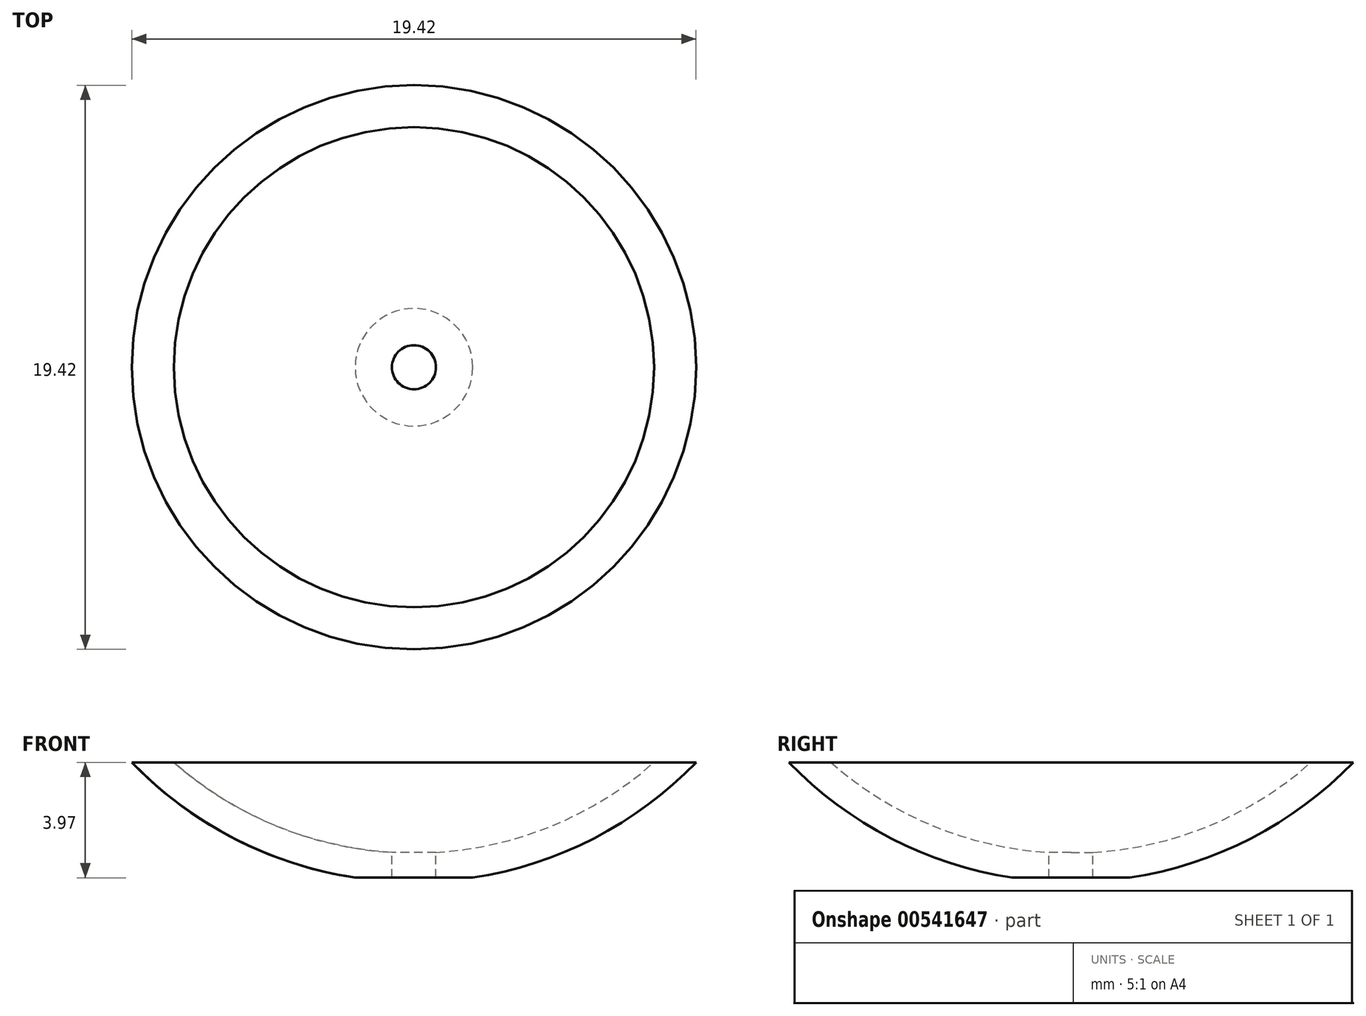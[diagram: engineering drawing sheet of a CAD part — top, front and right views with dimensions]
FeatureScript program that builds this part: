
annotation { "Feature Type Name" : "Feature", "Feature Type Description" : "" }
export const myFeature = defineFeature(function(context is Context, id is Id, definition is map)
    precondition{}
    {
        {
            var Q0;
            Q0=qCreatedBy(makeId("Front.planeOp"),FACE);
            var sketch = newSketch(context, id + "F0", { "sketchPlane" : qUnion([Q0])});
            skCircle(sketch, "E0", {"center": v(0, 0) * mm, "radius": 13.5 * mm});
            skLineSegment(sketch, "E1", {"start": v(0, 13.5) * mm, "end": v(0, -13.5) * mm});
            skSolve(sketch);
        }
        {
            var Q0;
            {var subQ0=sQuery(id+"F0.wireOp",EDGE,"E1");Q0=makeQuery(id+"F0.imprint","IMPRINT",FACE,{"disambiguationData":[TD([[makeQuery(id+"F0.imprint","IMPRINT",EDGE,{"derivedFrom":subQ0}),1.0]])]});}
            var Q1;
            Q1=sQuery(id+"F0.wireOp",EDGE,"E1");
            revolve(context, id + "F1", {"entities" : qUnion([Q0]), "axis" : qUnion([Q1]), "revolveType" : RevolveType.FULL});
        }
        {
            var Q0;
            Q0=qCreatedBy(makeId("Front.planeOp"),FACE);
            var sketch = newSketch(context, id + "F2", { "sketchPlane" : qUnion([Q0])});
            skLineSegment(sketch, "E2.bottom", {"start": v(-19.86, 24.4) * mm, "end": v(21.18, 24.4) * mm});
            skLineSegment(sketch, "E2.top", {"start": v(-19.86, -21.72) * mm, "end": v(21.18, -21.72) * mm});
            skLineSegment(sketch, "E2.left", {"start": v(-19.86, 24.4) * mm, "end": v(-19.86, -21.72) * mm});
            skLineSegment(sketch, "E2.right", {"start": v(21.18, 24.4) * mm, "end": v(21.18, -21.72) * mm});
            skLineSegment(sketch, "E3", {"start": v(-19.86, -9.38) * mm, "end": v(21.18, -9.38) * mm});
            skSolve(sketch);
        }
        {
            var Q0;
            {var subQ0=sQuery(id+"F2.wireOp",EDGE,"E2.bottom");Q0=makeQuery(id+"F2.imprint","IMPRINT",FACE,{"disambiguationData":[TD([[makeQuery(id+"F2.imprint","IMPRINT",EDGE,{"derivedFrom":subQ0}),-1.0]])]});}
            extrude(context, id + "F3", {"entities" : qUnion([Q0]), "operationType" : NewBodyOperationType.REMOVE, "endBound" : BoundingType.SYMMETRIC, "oppositeDirection" : true, "depth" : 50.8 * mm, "offsetDistance" : 25.4 * mm});
        }
        {
            var Q0;
            Q0=makeQuery(id+"F3.boolean.opBoolean","COPY",FACE,{"derivedFrom":makeQuery(id+"F3.opExtrude","SWEPT_FACE",FACE,{"disambiguationData":[OSD([sQuery(id+"F2.wireOp",EDGE,"E3")])]})});
            shell(context, id + "F4", {"entities" : qUnion([Q0]), "thickness" : 1 * mm});
        }
        {
            var Q0;
            Q0=qCreatedBy(makeId("Front.planeOp"),FACE);
            var sketch = newSketch(context, id + "F5", { "sketchPlane" : qUnion([Q0])});
            skLineSegment(sketch, "E4.bottom", {"start": v(-8, -14.98) * mm, "end": v(7.64, -14.98) * mm});
            skLineSegment(sketch, "E4.top", {"start": v(-8, -13.35) * mm, "end": v(7.64, -13.35) * mm});
            skLineSegment(sketch, "E4.left", {"start": v(-8, -14.98) * mm, "end": v(-8, -13.35) * mm});
            skLineSegment(sketch, "E4.right", {"start": v(7.64, -14.98) * mm, "end": v(7.64, -13.35) * mm});
            skSolve(sketch);
        }
        {
            var Q0;
            Q0=makeQuery(id+"F5.imprint","IMPRINT",FACE,{"disambiguationData":[TD([[makeQuery(id+"F5.imprint","IMPRINT",EDGE,{"derivedFrom":sQuery(id+"F5.wireOp",EDGE,"E4.bottom")}),1.0]])]});
            extrude(context, id + "F6", {"entities" : qUnion([Q0]), "operationType" : NewBodyOperationType.REMOVE, "endBound" : BoundingType.SYMMETRIC, "oppositeDirection" : true, "depth" : 25.4 * mm, "offsetDistance" : 25.4 * mm});
        }
        {
            var Q0;
            Q0=qCreatedBy(makeId("Top.planeOp"),FACE);
            var sketch = newSketch(context, id + "F7", { "sketchPlane" : qUnion([Q0])});
            skCircle(sketch, "E5", {"center": v(0, 0) * mm, "radius": 0.76 * mm});
            skSolve(sketch);
        }
        {
            var Q0;
            Q0=makeQuery(id+"F7.imprint","IMPRINT",FACE,{"disambiguationData":[TD([[makeQuery(id+"F7.imprint","IMPRINT",EDGE,{"derivedFrom":sQuery(id+"F7.wireOp",EDGE,"E5")}),1.0]])]});
            extrude(context, id + "F8", {"entities" : qUnion([Q0]), "operationType" : NewBodyOperationType.REMOVE, "oppositeDirection" : true, "depth" : 25.4 * mm, "offsetDistance" : 25.4 * mm});
        }
    });
